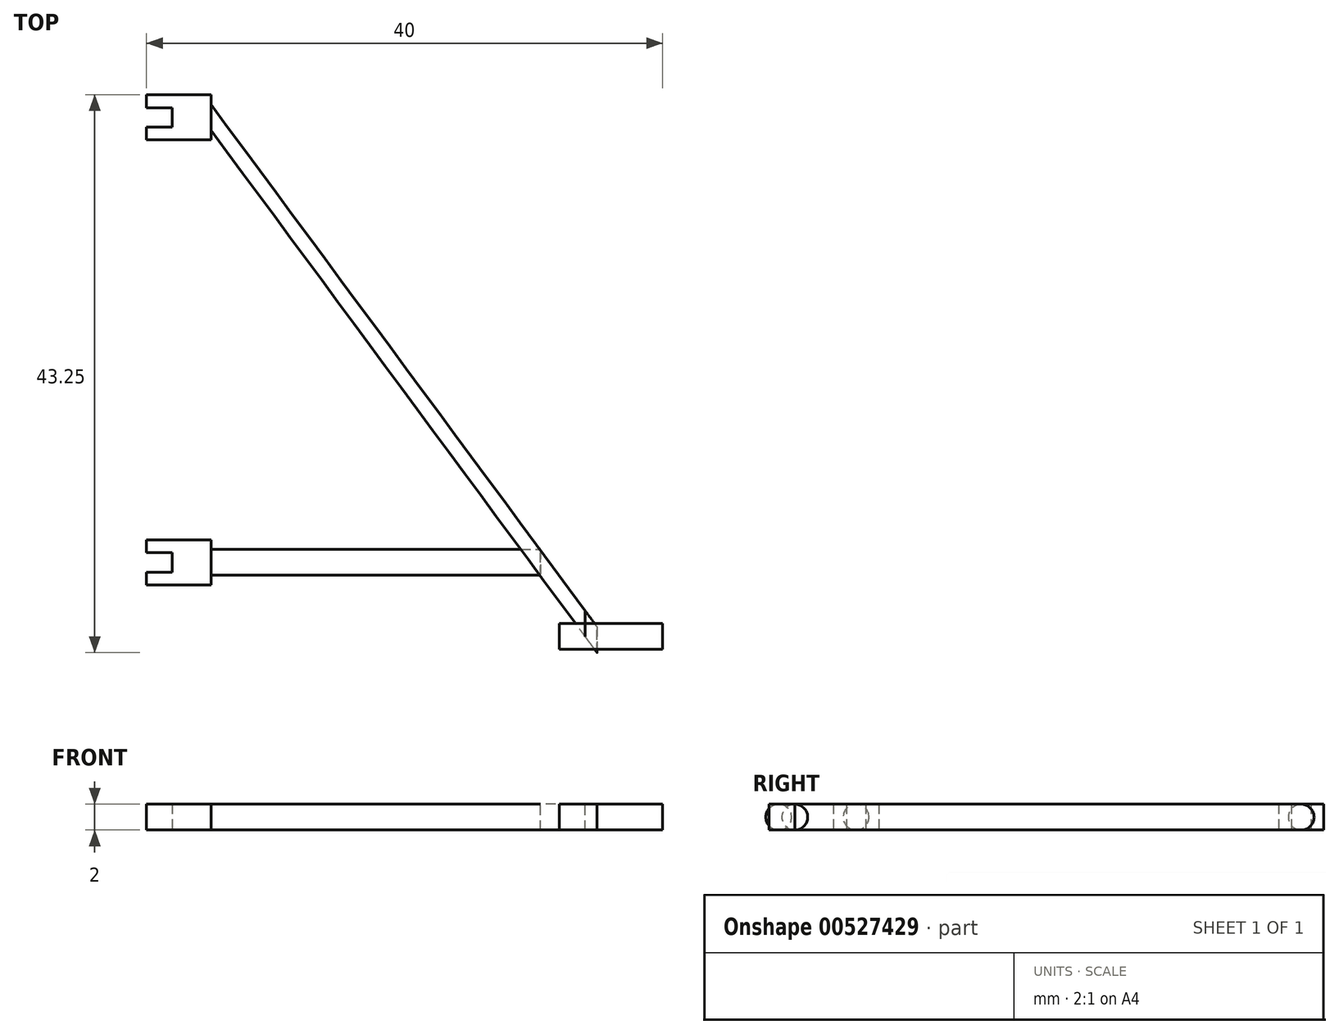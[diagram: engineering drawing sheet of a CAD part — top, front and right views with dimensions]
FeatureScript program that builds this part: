
annotation { "Feature Type Name" : "Feature", "Feature Type Description" : "" }
export const myFeature = defineFeature(function(context is Context, id is Id, definition is map)
    precondition{}
    {
        {
            var Q0;
            Q0=qCreatedBy(makeId("Top.planeOp"),FACE);
            var sketch = newSketch(context, id + "F0", { "sketchPlane" : qUnion([Q0])});
            skLineSegment(sketch, "E0", {"start": v(14.15, 54.75) * mm, "end": v(14.15, 53.75) * mm});
            skLineSegment(sketch, "E1", {"start": v(14.15, 53.75) * mm, "end": v(16.15, 53.75) * mm});
            skLineSegment(sketch, "E2", {"start": v(16.15, 53.75) * mm, "end": v(16.15, 52.25) * mm});
            skLineSegment(sketch, "E3", {"start": v(16.15, 52.25) * mm, "end": v(14.15, 52.25) * mm});
            skLineSegment(sketch, "E4", {"start": v(14.15, 52.25) * mm, "end": v(14.15, 51.25) * mm});
            skLineSegment(sketch, "E5", {"start": v(14.15, 51.25) * mm, "end": v(19.15, 51.25) * mm});
            skLineSegment(sketch, "E6", {"start": v(19.15, 51.25) * mm, "end": v(19.15, 54.75) * mm});
            skLineSegment(sketch, "E7", {"start": v(19.15, 54.75) * mm, "end": v(14.15, 54.75) * mm});
            skLineSegment(sketch, "E8", {"start": v(16.15, 52.25) * mm, "end": v(16.15, 19.25) * mm, "construction": true});
            skLineSegment(sketch, "E9", {"start": v(16.15, 35.75) * mm, "end": v(4.32, 35.75) * mm, "construction": true});
            skPoint(sketch, "E9.endSnap0", {"position": v(16.15, 35.75) * mm});
            skLineSegment(sketch, "E10.MirrorCS", {"start": v(19.15, 16.75) * mm, "end": v(14.15, 16.75) * mm});
            skLineSegment(sketch, "E11.MirrorCS", {"start": v(14.15, 16.75) * mm, "end": v(14.15, 17.75) * mm});
            skLineSegment(sketch, "E12.MirrorCS", {"start": v(14.15, 17.75) * mm, "end": v(16.15, 17.75) * mm});
            skLineSegment(sketch, "E13.MirrorCS", {"start": v(16.15, 17.75) * mm, "end": v(16.15, 19.25) * mm});
            skLineSegment(sketch, "E14.MirrorCS", {"start": v(16.15, 19.25) * mm, "end": v(14.15, 19.25) * mm});
            skLineSegment(sketch, "E15.MirrorCS", {"start": v(14.15, 19.25) * mm, "end": v(14.15, 20.25) * mm});
            skLineSegment(sketch, "E16.MirrorCS", {"start": v(14.15, 20.25) * mm, "end": v(19.15, 20.25) * mm});
            skLineSegment(sketch, "E17.MirrorCS", {"start": v(19.15, 20.25) * mm, "end": v(19.15, 16.75) * mm});
            skLineSegment(sketch, "E18", {"start": v(16.15, 17.75) * mm, "end": v(16.15, 11.75) * mm, "construction": true});
            skLineSegment(sketch, "E19", {"start": v(16.15, 11.75) * mm, "end": v(46.15, 11.75) * mm, "construction": true});
            skLineSegment(sketch, "E20", {"start": v(46.15, 11.75) * mm, "end": v(54.15, 11.75) * mm});
            skLineSegment(sketch, "E21", {"start": v(54.15, 11.75) * mm, "end": v(54.15, 13.75) * mm});
            skLineSegment(sketch, "E22", {"start": v(54.15, 13.75) * mm, "end": v(46.15, 13.75) * mm});
            skLineSegment(sketch, "E23", {"start": v(46.15, 13.75) * mm, "end": v(46.15, 11.75) * mm});
            skSolve(sketch);
        }
        {
            var Q0;
            Q0 = qSketchRegion(id + "F0", true);
            extrude(context, id + "F1", {"entities" : qUnion([Q0]), "depth" : 2 * mm, "offsetDistance" : 25 * mm});
        }
        {
            var Q0;
            Q0=qCreatedBy(makeId("Top.planeOp"),FACE);
            cPlane(context, id + "F2", {"entities" : qUnion([Q0]), "cplaneType" : CPlaneType.OFFSET, "offset" : 1 * mm, "width" : 150 * mm, "height" : 150 * mm});
        }
        {
            var Q0;
            Q0 = qSketchRegion(id + "F0", true);
            extrude(context, id + "F3", {"entities" : qUnion([Q0]), "depth" : 2 * mm, "offsetDistance" : 25 * mm});
        }
        {
            var Q0;
            Q0=makeQuery(id+"F1.opExtrude","SWEPT_FACE",FACE,{"disambiguationData":[OSD([sQuery(id+"F0.wireOp",EDGE,"E6")])]});
            var sketch = newSketch(context, id + "F4", { "sketchPlane" : qUnion([Q0])});
            skCircle(sketch, "E24", {"center": v(53, 1) * mm, "radius": 1 * mm});
            skPoint(sketch, "E24.centerSnap0", {"position": v(51.25, 1) * mm});
            skPoint(sketch, "E24.centerSnap1", {"position": v(53, 2) * mm});
            skSolve(sketch);
        }
        {
            var Q0;
            Q0=makeQuery(id+"F1.opExtrude","SWEPT_FACE",FACE,{"disambiguationData":[OSD([sQuery(id+"F0.wireOp",EDGE,"E17.MirrorCS")])]});
            var sketch = newSketch(context, id + "F5", { "sketchPlane" : qUnion([Q0])});
            skCircle(sketch, "E25", {"center": v(18.5, 1) * mm, "radius": 1 * mm});
            skPoint(sketch, "E25.centerSnap0", {"position": v(18.5, 2) * mm});
            skPoint(sketch, "E25.centerSnap1", {"position": v(16.75, 1) * mm});
            skSolve(sketch);
        }
        {
            var Q0;
            Q0=makeQuery(id+"F1.opExtrude","SWEPT_FACE",FACE,{"disambiguationData":[OSD([sQuery(id+"F0.wireOp",EDGE,"E22")])]});
            var sketch = newSketch(context, id + "F6", { "sketchPlane" : qUnion([Q0])});
            skLineSegment(sketch, "E26", {"start": v(-46.15, 1) * mm, "end": v(-48.15, 1) * mm, "construction": true});
            skCircle(sketch, "E27", {"center": v(-48.15, 1) * mm, "radius": 1 * mm});
            skSolve(sketch);
        }
        {
            var Q0;
            Q0=qCreatedBy(id+"F2.planeOp",FACE);
            var sketch = newSketch(context, id + "F7", { "sketchPlane" : qUnion([Q0])});
            skPoint(sketch, "E28.0", {"position": v(19.15, 53) * mm});
            skPoint(sketch, "E29.0", {"position": v(48.15, 13.75) * mm});
            skPoint(sketch, "E30.0", {"position": v(19.15, 18.5) * mm});
            skLineSegment(sketch, "E31", {"start": v(19.15, 53) * mm, "end": v(48.15, 13.75) * mm});
            skLineSegment(sketch, "E32", {"start": v(48.15, 13.75) * mm, "end": v(48.62, 13.11) * mm});
            skLineSegment(sketch, "E33", {"start": v(19.15, 18.5) * mm, "end": v(43.6, 18.5) * mm});
            skLineSegment(sketch, "E34", {"start": v(48.62, 13.11) * mm, "end": v(49.07, 12.5) * mm});
            skSolve(sketch);
        }
        {
            var Q0;
            {var subQ0=sQuery(id+"F4.wireOp",EDGE,"E24");var subQ1=sQuery(id+"F0.wireOp",EDGE,"E6");var subQ2=makeQuery(id+"F4.imprint","INTERSECT",VERTEX,{"derivedFrom":[makeQuery(id+"F1.opExtrude","CAP_EDGE",EDGE,{"disambiguationData":[OSD([subQ1])],"isStart":true}),subQ0]});Q0=makeQuery(id+"F4.imprint","IMPRINT",FACE,{"disambiguationData":[TD([[makeQuery(id+"F4.imprint","IMPRINT",EDGE,{"disambiguationData":[TD([[subQ2,1.0]])],"derivedFrom":subQ0}),1.0]])]});}
            var Q1;
            Q1=sQuery(id+"F7.wireOp",EDGE,"E31");
            var Q2;
            Q2=sQuery(id+"F7.wireOp",EDGE,"E32");
            var Q3;
            Q3=sQuery(id+"F7.wireOp",EDGE,"E34");
            sweep(context, id + "F8", {"profiles" : qUnion([Q0]), "path" : qUnion([Q1, Q2, Q3])});
        }
        {
            var Q0;
            Q0=qCreatedBy(id+"F2.planeOp",FACE);
            var sketch = newSketch(context, id + "F9", { "sketchPlane" : qUnion([Q0])});
            skPoint(sketch, "E35.0", {"position": v(19.15, 18.5) * mm});
            skLineSegment(sketch, "E36", {"start": v(19.15, 18.5) * mm, "end": v(44.67, 18.5) * mm});
            skSolve(sketch);
        }
        {
            var Q0;
            {var subQ0=sQuery(id+"F5.wireOp",EDGE,"E25");var subQ1=sQuery(id+"F0.wireOp",EDGE,"E17.MirrorCS");var subQ2=makeQuery(id+"F5.imprint","INTERSECT",VERTEX,{"derivedFrom":[makeQuery(id+"F1.opExtrude","CAP_EDGE",EDGE,{"disambiguationData":[OSD([subQ1])],"isStart":true}),subQ0]});Q0=makeQuery(id+"F5.imprint","IMPRINT",FACE,{"disambiguationData":[TD([[makeQuery(id+"F5.imprint","IMPRINT",EDGE,{"disambiguationData":[TD([[subQ2,1.0]])],"derivedFrom":subQ0}),1.0]])]});}
            var Q1;
            Q1=sQuery(id+"F9.wireOp",EDGE,"E36");
            sweep(context, id + "F10", {"profiles" : qUnion([Q0]), "path" : qUnion([Q1])});
        }
    });
